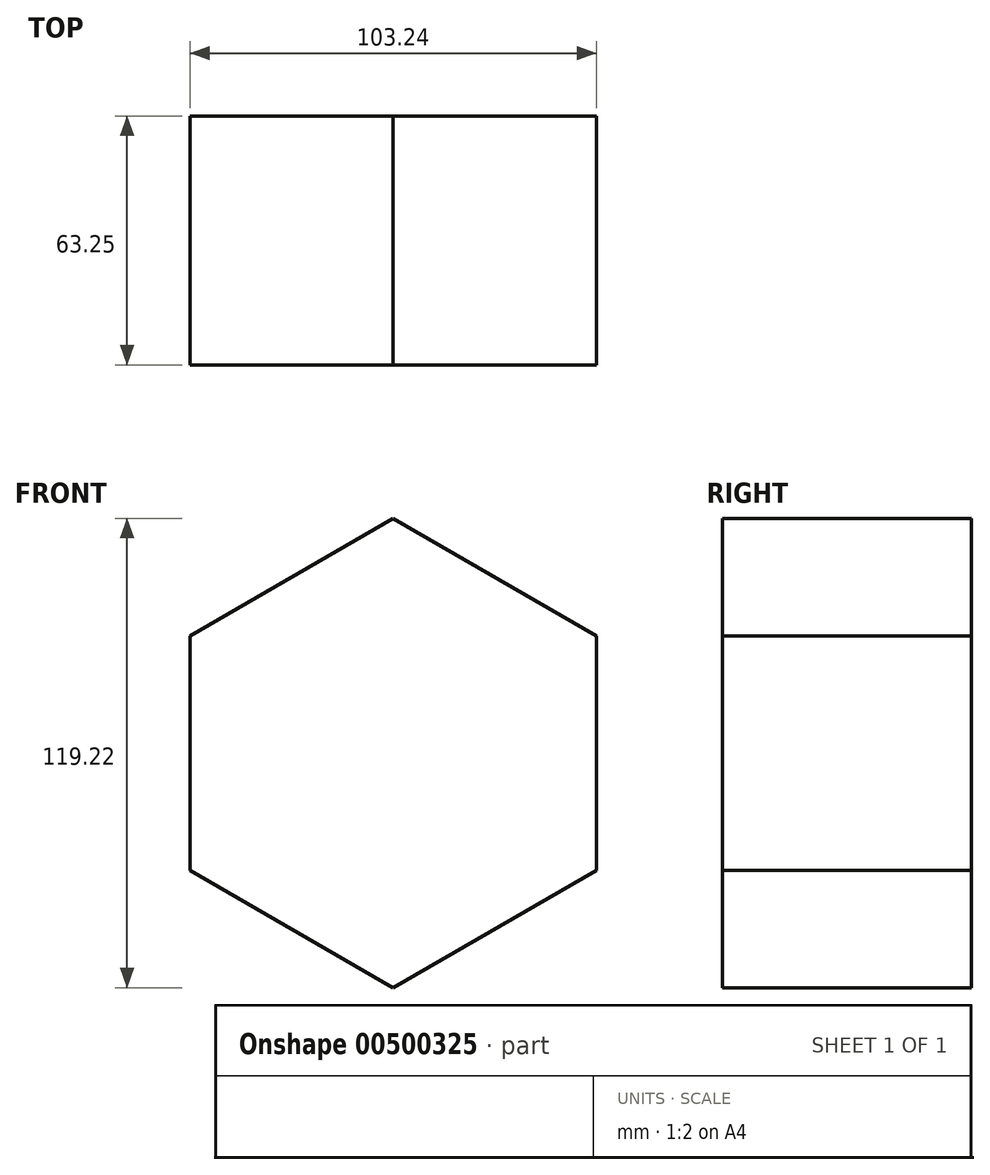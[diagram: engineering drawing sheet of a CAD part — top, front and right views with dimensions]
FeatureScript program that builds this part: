
annotation { "Feature Type Name" : "Feature", "Feature Type Description" : "" }
export const myFeature = defineFeature(function(context is Context, id is Id, definition is map)
    precondition{}
    {
        {
            var Q0;
            Q0=qCreatedBy(makeId("Front.planeOp"),FACE);
            var sketch = newSketch(context, id + "F0", { "sketchPlane" : qUnion([Q0])});
            skCircle(sketch, "E0.cCircle", {"center": v(0, 0) * mm, "radius": 59.6 * mm, "construction": true});
            skLineSegment(sketch, "E0.0", {"start": v(0, 59.6) * mm, "end": v(51.62, 29.8) * mm});
            skLineSegment(sketch, "E0.1", {"start": v(51.62, 29.8) * mm, "end": v(51.62, -29.8) * mm});
            skLineSegment(sketch, "E0.2", {"start": v(51.62, -29.8) * mm, "end": v(0, -59.6) * mm});
            skLineSegment(sketch, "E0.3", {"start": v(0, -59.6) * mm, "end": v(-51.62, -29.8) * mm});
            skLineSegment(sketch, "E0.4", {"start": v(-51.62, -29.8) * mm, "end": v(-51.62, 29.8) * mm});
            skLineSegment(sketch, "E0.5", {"start": v(-51.62, 29.8) * mm, "end": v(0, 59.6) * mm});
            skSolve(sketch);
        }
        {
            var Q0;
            Q0 = qSketchRegion(id + "F0", true);
            extrude(context, id + "F1", {"entities" : qUnion([Q0]), "depth" : 63.25 * mm});
        }
    });
